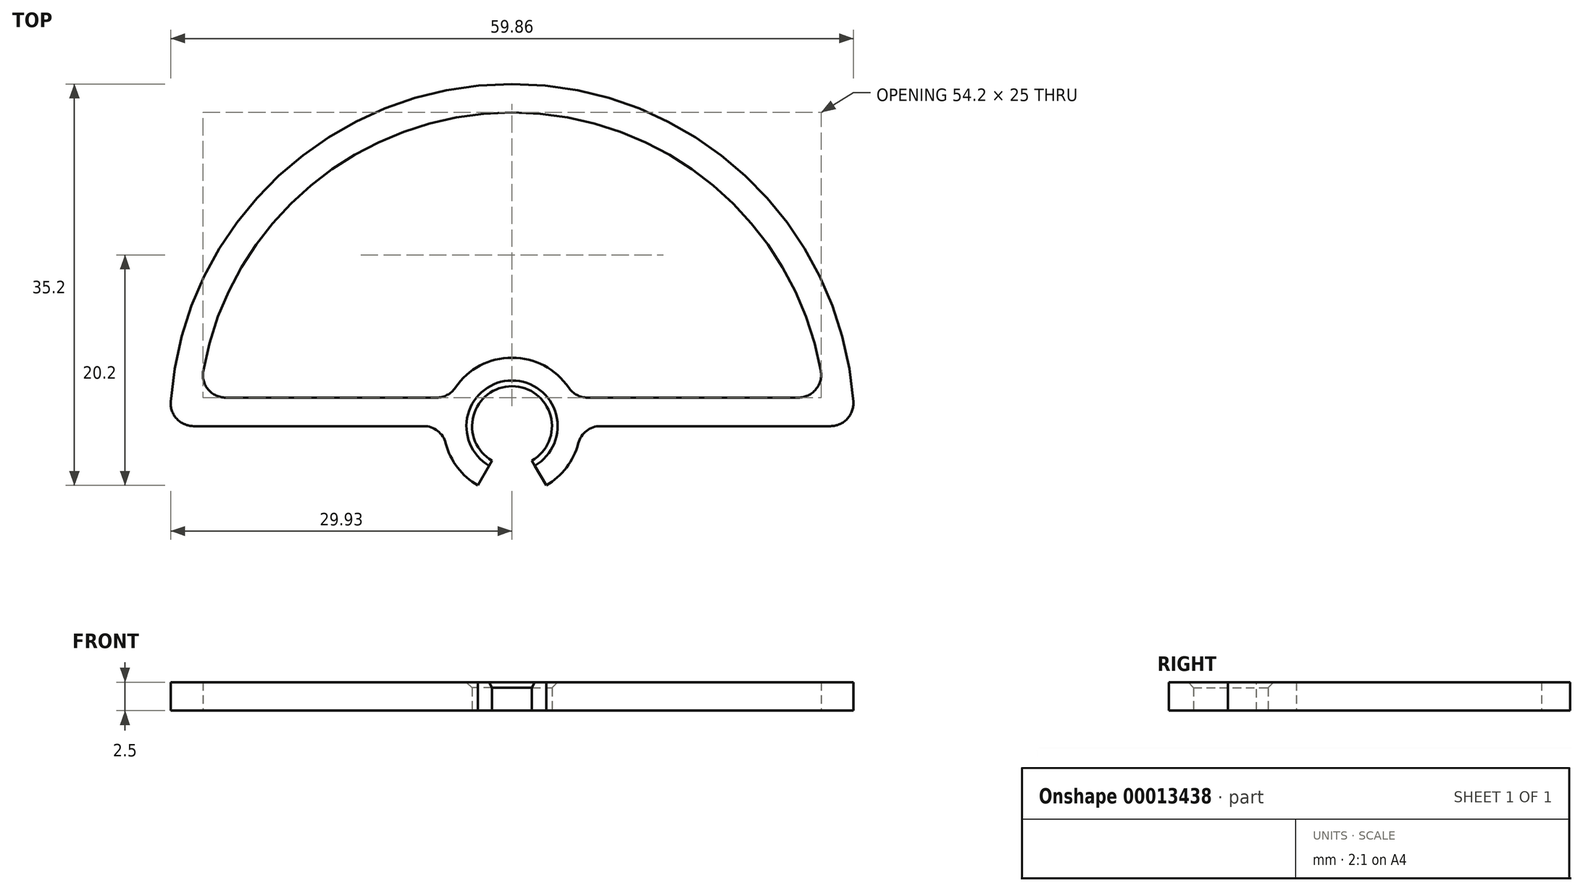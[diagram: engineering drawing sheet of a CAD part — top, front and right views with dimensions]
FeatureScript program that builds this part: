
annotation { "Feature Type Name" : "Feature", "Feature Type Description" : "" }
export const myFeature = defineFeature(function(context is Context, id is Id, definition is map)
    precondition{}
    {
        {
            var Q0;
            Q0=qCreatedBy(makeId("Top.planeOp"),FACE);
            var sketch = newSketch(context, id + "F0", { "sketchPlane" : qUnion([Q0])});
            skCircle(sketch, "E0", {"center": v(0, 0) * mm, "radius": 3.5 * mm});
            skArc(sketch, "E1", {"start": v(30, 0) * mm, "mid": v(0, 30) * mm, "end": v(-30, 0) * mm});
            skLineSegment(sketch, "E2", {"start": v(-30, 0) * mm, "end": v(30, 0) * mm});
            skArc(sketch, "E3.0", {"start": v(27.39, 2.5) * mm, "mid": v(0, 27.5) * mm, "end": v(-27.39, 2.5) * mm});
            skLineSegment(sketch, "E3.1", {"start": v(-27.39, 2.5) * mm, "end": v(27.39, 2.5) * mm});
            skLineSegment(sketch, "E4", {"start": v(0, 0) * mm, "end": v(-3, -5.2) * mm});
            skLineSegment(sketch, "E5", {"start": v(0, 0) * mm, "end": v(3, -5.2) * mm});
            skCircle(sketch, "E6", {"center": v(0, 0) * mm, "radius": 6 * mm});
            skLineSegment(sketch, "E7", {"start": v(0, 27.5) * mm, "end": v(0, 30) * mm, "construction": true});
            skLineSegment(sketch, "E8", {"start": v(0, 3.5) * mm, "end": v(0, 6) * mm, "construction": true});
            skSolve(sketch);
        }
        {
            var Q0;
            {var subQ12=sQuery(id+"F0.wireOp",EDGE,"E1");Q0=makeQuery(id+"F0.imprint","IMPRINT",FACE,{"disambiguationData":[TD([[makeQuery(id+"F0.imprint","IMPRINT",EDGE,{"derivedFrom":subQ12}),1.0]])]});}
            var Q1;
            {var subQ2=sQuery(id+"F0.wireOp",EDGE,"8d228c2e-07d6-44f8-8097-59b8630ab0c5");Q1=makeQuery(id+"F0.imprint","IMPRINT",FACE,{"disambiguationData":[TD([[makeQuery(id+"F0.imprint","IMPRINT",EDGE,{"derivedFrom":subQ2}),-1.0]])]});}
            var Q2;
            {var subQ0=sQuery(id+"F0.wireOp",EDGE,"E3.1");var subQ3=sQuery(id+"F0.wireOp",EDGE,"E0");var subQ4=makeQuery(id+"F0.imprint","INTERSECT",VERTEX,{"disambiguationData":[OD(0.0)],"derivedFrom":[subQ3,subQ0]});Q2=makeQuery(id+"F0.imprint","IMPRINT",FACE,{"disambiguationData":[TD([[makeQuery(id+"F0.imprint","IMPRINT",EDGE,{"disambiguationData":[TD([[subQ4,-1.0]])],"derivedFrom":subQ3}),-1.0]])]});}
            var Q3;
            {var subQ0=sQuery(id+"F0.wireOp",EDGE,"E3.1");var subQ3=sQuery(id+"F0.wireOp",EDGE,"E0");var subQ4=makeQuery(id+"F0.imprint","INTERSECT",VERTEX,{"disambiguationData":[OD(1.0)],"derivedFrom":[subQ3,subQ0]});Q3=makeQuery(id+"F0.imprint","IMPRINT",FACE,{"disambiguationData":[TD([[makeQuery(id+"F0.imprint","IMPRINT",EDGE,{"disambiguationData":[TD([[subQ4,-1.0]])],"derivedFrom":subQ3}),-1.0]])]});}
            var Q4;
            {var subQ0=sQuery(id+"F0.wireOp",EDGE,"E3.1");var subQ3=sQuery(id+"F0.wireOp",EDGE,"E0");var subQ4=makeQuery(id+"F0.imprint","INTERSECT",VERTEX,{"disambiguationData":[OD(0.0)],"derivedFrom":[subQ3,subQ0]});Q4=makeQuery(id+"F0.imprint","IMPRINT",FACE,{"disambiguationData":[TD([[makeQuery(id+"F0.imprint","IMPRINT",EDGE,{"disambiguationData":[TD([[subQ4,1.0]])],"derivedFrom":subQ3}),-1.0]])]});}
            var Q5;
            {var subQ1=sQuery(id+"F0.wireOp",EDGE,"E2");var subQ5=sQuery(id+"F0.wireOp",EDGE,"E0");var subQ7=makeQuery(id+"F0.imprint","INTERSECT",VERTEX,{"disambiguationData":[OD(0.0)],"derivedFrom":[subQ5,subQ1]});Q5=makeQuery(id+"F0.imprint","IMPRINT",FACE,{"disambiguationData":[TD([[makeQuery(id+"F0.imprint","IMPRINT",EDGE,{"disambiguationData":[TD([[subQ7,1.0]])],"derivedFrom":subQ5}),-1.0]])]});}
            var Q6;
            {var subQ1=sQuery(id+"F0.wireOp",EDGE,"E0");var subQ5=sQuery(id+"F0.wireOp",EDGE,"E2");var subQ7=makeQuery(id+"F0.imprint","INTERSECT",VERTEX,{"disambiguationData":[OD(1.0)],"derivedFrom":[subQ1,subQ5]});Q6=makeQuery(id+"F0.imprint","IMPRINT",FACE,{"disambiguationData":[TD([[makeQuery(id+"F0.imprint","IMPRINT",EDGE,{"disambiguationData":[TD([[subQ7,-1.0]])],"derivedFrom":subQ1}),-1.0]])]});}
            var Q7;
            {var subQ0=sQuery(id+"F0.wireOp",EDGE,"39a22298-869b-4f79-8d30-5df6fd3aea0c");Q7=makeQuery(id+"F0.imprint","IMPRINT",FACE,{"disambiguationData":[TD([[makeQuery(id+"F0.imprint","IMPRINT",EDGE,{"derivedFrom":subQ0}),-1.0]])]});}
            extrude(context, id + "F1", {"entities" : qUnion([Q0, Q1, Q2, Q3, Q4, Q5, Q6, Q7]), "depth" : 2.5 * mm});
        }
        {
            var Q0;
            Q0=makeQuery(id+"F1.opExtrude","CAP_EDGE",EDGE,{"disambiguationData":[OSD([sQuery(id+"F0.wireOp",EDGE,"E0")])],"isStart":false});
            chamfer(context, id + "F2", {"entities" : qUnion([Q0]), "width" : .5 * mm, "tangentPropagation" : true});
        }
        {
            var Q0;
            {var subQ0=sQuery(id+"F0.wireOp",EDGE,"E2");var subQ1=sQuery(id+"F0.wireOp",EDGE,"E6");Q0=makeQuery(id+"F1.opExtrude","SWEPT_EDGE",EDGE,{"disambiguationData":[OSD([subQ0,subQ1]),TDD([makeQuery(id+"F0.imprint","INTERSECT",VERTEX,{"disambiguationData":[OD(0.0)],"derivedFrom":[subQ0,subQ1]})])]});}
            var Q1;
            {var subQ0=sQuery(id+"F0.wireOp",EDGE,"E2");var subQ1=sQuery(id+"F0.wireOp",EDGE,"E6");Q1=makeQuery(id+"F1.opExtrude","SWEPT_EDGE",EDGE,{"disambiguationData":[OSD([subQ0,subQ1]),TDD([makeQuery(id+"F0.imprint","INTERSECT",VERTEX,{"disambiguationData":[OD(1.0)],"derivedFrom":[subQ0,subQ1]})])]});}
            var Q2;
            {var subQ0=sQuery(id+"F0.wireOp",EDGE,"E3.1");var subQ1=sQuery(id+"F0.wireOp",EDGE,"E6");Q2=makeQuery(id+"F1.opExtrude","SWEPT_EDGE",EDGE,{"disambiguationData":[OSD([subQ0,subQ1]),TDD([makeQuery(id+"F0.imprint","INTERSECT",VERTEX,{"disambiguationData":[OD(0.0)],"derivedFrom":[subQ0,subQ1]})])]});}
            var Q3;
            {var subQ0=sQuery(id+"F0.wireOp",EDGE,"E3.1");var subQ1=sQuery(id+"F0.wireOp",EDGE,"E6");Q3=makeQuery(id+"F1.opExtrude","SWEPT_EDGE",EDGE,{"disambiguationData":[OSD([subQ0,subQ1]),TDD([makeQuery(id+"F0.imprint","INTERSECT",VERTEX,{"disambiguationData":[OD(1.0)],"derivedFrom":[subQ0,subQ1]})])]});}
            var Q4;
            {var subQ0=sQuery(id+"F0.wireOp",EDGE,"E2");var subQ1=sQuery(id+"F0.wireOp",EDGE,"E6");Q4=makeQuery(id+"F1.opExtrude","SWEPT_EDGE",EDGE,{"disambiguationData":[OSD([subQ0,subQ1]),TDD([makeQuery(id+"F0.imprint","INTERSECT",VERTEX,{"disambiguationData":[OD(0.0)],"derivedFrom":[subQ0,subQ1]})])]});}
            var Q5;
            {var subQ0=sQuery(id+"F0.wireOp",EDGE,"E2");var subQ1=sQuery(id+"F0.wireOp",EDGE,"E6");Q5=makeQuery(id+"F1.opExtrude","SWEPT_EDGE",EDGE,{"disambiguationData":[OSD([subQ0,subQ1]),TDD([makeQuery(id+"F0.imprint","INTERSECT",VERTEX,{"disambiguationData":[OD(1.0)],"derivedFrom":[subQ0,subQ1]})])]});}
            var Q6;
            {var subQ0=sQuery(id+"F0.wireOp",EDGE,"E3.1");var subQ1=sQuery(id+"F0.wireOp",EDGE,"E6");Q6=makeQuery(id+"F1.opExtrude","SWEPT_EDGE",EDGE,{"disambiguationData":[OSD([subQ0,subQ1]),TDD([makeQuery(id+"F0.imprint","INTERSECT",VERTEX,{"disambiguationData":[OD(0.0)],"derivedFrom":[subQ0,subQ1]})])]});}
            var Q7;
            {var subQ0=sQuery(id+"F0.wireOp",EDGE,"E3.1");var subQ1=sQuery(id+"F0.wireOp",EDGE,"E6");Q7=makeQuery(id+"F1.opExtrude","SWEPT_EDGE",EDGE,{"disambiguationData":[OSD([subQ0,subQ1]),TDD([makeQuery(id+"F0.imprint","INTERSECT",VERTEX,{"disambiguationData":[OD(1.0)],"derivedFrom":[subQ0,subQ1]})])]});}
            var Q8;
            {var subQ0=sQuery(id+"F0.wireOp",EDGE,"E1");var subQ1=sQuery(id+"F0.wireOp",EDGE,"E2");Q8=makeQuery(id+"F1.opExtrude","SWEPT_EDGE",EDGE,{"disambiguationData":[OSD([subQ0,subQ1]),TDD([makeQuery(id+"F0.imprint","INTERSECT",VERTEX,{"disambiguationData":[OD(1.0)],"derivedFrom":[subQ0,subQ1]})])]});}
            var Q9;
            {var subQ0=sQuery(id+"F0.wireOp",EDGE,"E1");var subQ1=sQuery(id+"F0.wireOp",EDGE,"E2");Q9=makeQuery(id+"F1.opExtrude","SWEPT_EDGE",EDGE,{"disambiguationData":[OSD([subQ0,subQ1]),TDD([makeQuery(id+"F0.imprint","INTERSECT",VERTEX,{"disambiguationData":[OD(0.0)],"derivedFrom":[subQ0,subQ1]})])]});}
            var Q10;
            {var subQ0=sQuery(id+"F0.wireOp",EDGE,"E3.0");var subQ1=sQuery(id+"F0.wireOp",EDGE,"E3.1");Q10=makeQuery(id+"F1.opExtrude","SWEPT_EDGE",EDGE,{"disambiguationData":[OSD([subQ0,subQ1]),TDD([makeQuery(id+"F0.imprint","INTERSECT",VERTEX,{"disambiguationData":[OD(0.0)],"derivedFrom":[subQ0,subQ1]})])]});}
            var Q11;
            {var subQ0=sQuery(id+"F0.wireOp",EDGE,"E3.0");var subQ1=sQuery(id+"F0.wireOp",EDGE,"E3.1");Q11=makeQuery(id+"F1.opExtrude","SWEPT_EDGE",EDGE,{"disambiguationData":[OSD([subQ0,subQ1]),TDD([makeQuery(id+"F0.imprint","INTERSECT",VERTEX,{"disambiguationData":[OD(1.0)],"derivedFrom":[subQ0,subQ1]})])]});}
            var Q12;
            {var subQ0=sQuery(id+"F0.wireOp",EDGE,"E3.0");var subQ1=sQuery(id+"F0.wireOp",EDGE,"E3.1");Q12=makeQuery(id+"F1.opExtrude","SWEPT_EDGE",EDGE,{"disambiguationData":[OSD([subQ0,subQ1]),TDD([makeQuery(id+"F0.imprint","INTERSECT",VERTEX,{"disambiguationData":[OD(0.0)],"derivedFrom":[subQ0,subQ1]})])]});}
            var Q13;
            {var subQ0=sQuery(id+"F0.wireOp",EDGE,"E3.0");var subQ1=sQuery(id+"F0.wireOp",EDGE,"E3.1");Q13=makeQuery(id+"F1.opExtrude","SWEPT_EDGE",EDGE,{"disambiguationData":[OSD([subQ0,subQ1]),TDD([makeQuery(id+"F0.imprint","INTERSECT",VERTEX,{"disambiguationData":[OD(1.0)],"derivedFrom":[subQ0,subQ1]})])]});}
            var Q14;
            {var subQ0=sQuery(id+"F0.wireOp",EDGE,"E3.0");var subQ1=sQuery(id+"F0.wireOp",EDGE,"E3.1");Q14=makeQuery(id+"F1.opExtrude","SWEPT_EDGE",EDGE,{"disambiguationData":[OSD([subQ0,subQ1]),TDD([makeQuery(id+"F0.imprint","INTERSECT",VERTEX,{"disambiguationData":[OD(1.0)],"derivedFrom":[subQ0,subQ1]})])]});}
            var Q15;
            {var subQ0=sQuery(id+"F0.wireOp",EDGE,"E3.0");var subQ1=sQuery(id+"F0.wireOp",EDGE,"E3.1");Q15=makeQuery(id+"F1.opExtrude","SWEPT_EDGE",EDGE,{"disambiguationData":[OSD([subQ0,subQ1]),TDD([makeQuery(id+"F0.imprint","INTERSECT",VERTEX,{"disambiguationData":[OD(0.0)],"derivedFrom":[subQ0,subQ1]})])]});}
            var Q16;
            {var subQ0=sQuery(id+"F0.wireOp",EDGE,"E3.1");var subQ1=sQuery(id+"F0.wireOp",EDGE,"E6");Q16=makeQuery(id+"F1.opExtrude","SWEPT_EDGE",EDGE,{"disambiguationData":[OSD([subQ0,subQ1]),TDD([makeQuery(id+"F0.imprint","INTERSECT",VERTEX,{"disambiguationData":[OD(1.0)],"derivedFrom":[subQ0,subQ1]})])]});}
            var Q17;
            {var subQ0=sQuery(id+"F0.wireOp",EDGE,"E2");var subQ1=sQuery(id+"F0.wireOp",EDGE,"E6");Q17=makeQuery(id+"F1.opExtrude","SWEPT_EDGE",EDGE,{"disambiguationData":[OSD([subQ0,subQ1]),TDD([makeQuery(id+"F0.imprint","INTERSECT",VERTEX,{"disambiguationData":[OD(0.0)],"derivedFrom":[subQ0,subQ1]})])]});}
            var Q18;
            {var subQ0=sQuery(id+"F0.wireOp",EDGE,"E2");var subQ1=sQuery(id+"F0.wireOp",EDGE,"E6");Q18=makeQuery(id+"F1.opExtrude","SWEPT_EDGE",EDGE,{"disambiguationData":[OSD([subQ0,subQ1]),TDD([makeQuery(id+"F0.imprint","INTERSECT",VERTEX,{"disambiguationData":[OD(1.0)],"derivedFrom":[subQ0,subQ1]})])]});}
            var Q19;
            {var subQ0=sQuery(id+"F0.wireOp",EDGE,"E3.1");var subQ1=sQuery(id+"F0.wireOp",EDGE,"E6");Q19=makeQuery(id+"F1.opExtrude","SWEPT_EDGE",EDGE,{"disambiguationData":[OSD([subQ0,subQ1]),TDD([makeQuery(id+"F0.imprint","INTERSECT",VERTEX,{"disambiguationData":[OD(0.0)],"derivedFrom":[subQ0,subQ1]})])]});}
            var Q20;
            {var subQ0=sQuery(id+"F0.wireOp",EDGE,"E3.1");var subQ1=sQuery(id+"F0.wireOp",EDGE,"E6");Q20=makeQuery(id+"F1.opExtrude","SWEPT_EDGE",EDGE,{"disambiguationData":[OSD([subQ0,subQ1]),TDD([makeQuery(id+"F0.imprint","INTERSECT",VERTEX,{"disambiguationData":[OD(1.0)],"derivedFrom":[subQ0,subQ1]})])]});}
            var Q21;
            {var subQ0=sQuery(id+"F0.wireOp",EDGE,"E3.1");var subQ1=sQuery(id+"F0.wireOp",EDGE,"E6");Q21=makeQuery(id+"F1.opExtrude","SWEPT_EDGE",EDGE,{"disambiguationData":[OSD([subQ0,subQ1]),TDD([makeQuery(id+"F0.imprint","INTERSECT",VERTEX,{"disambiguationData":[OD(0.0)],"derivedFrom":[subQ0,subQ1]})])]});}
            fillet(context, id + "F3", {"entities" : qUnion([Q0, Q1, Q2, Q3, Q4, Q5, Q6, Q7, Q8, Q9, Q10, Q11, Q12, Q13, Q14, Q15, Q16, Q17, Q18, Q19, Q20, Q21]), "radius" : 2 * mm, "tangentPropagation" : true, "allowEdgeOverflow" : false});
        }
    });
